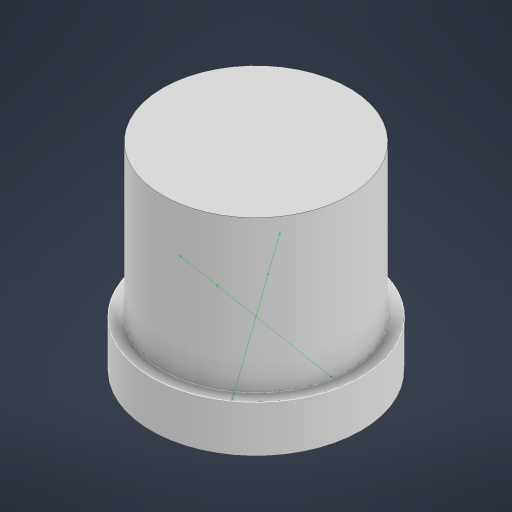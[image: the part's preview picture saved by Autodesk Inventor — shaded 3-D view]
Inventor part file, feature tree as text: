
AUTODESK INVENTOR PART (.ipt)
format: ipt  version: 2023 (Build 270158000, 158)  size: 170,496 bytes
history: native  units: mm
features: extrude x2, sketch x1
ambient origin geometry x8: Origin, YZ Plane, XZ Plane, XY Plane, X Axis, Y Axis, Z Axis, Center Point
bodies: Solid1 (feature_tree)
feature tree (3):
  sketch  "Sketch1"  dims[d0=9.0mm d1=8.0mm d2=6.5mm d3=0.0mm d4=2.0mm d5=0.0mm]
  extrude  "Extrusion1"  Depth=2.0mm
  extrude  "Extrusion2"  Depth=6.5mm TaperAngle=0.0deg
